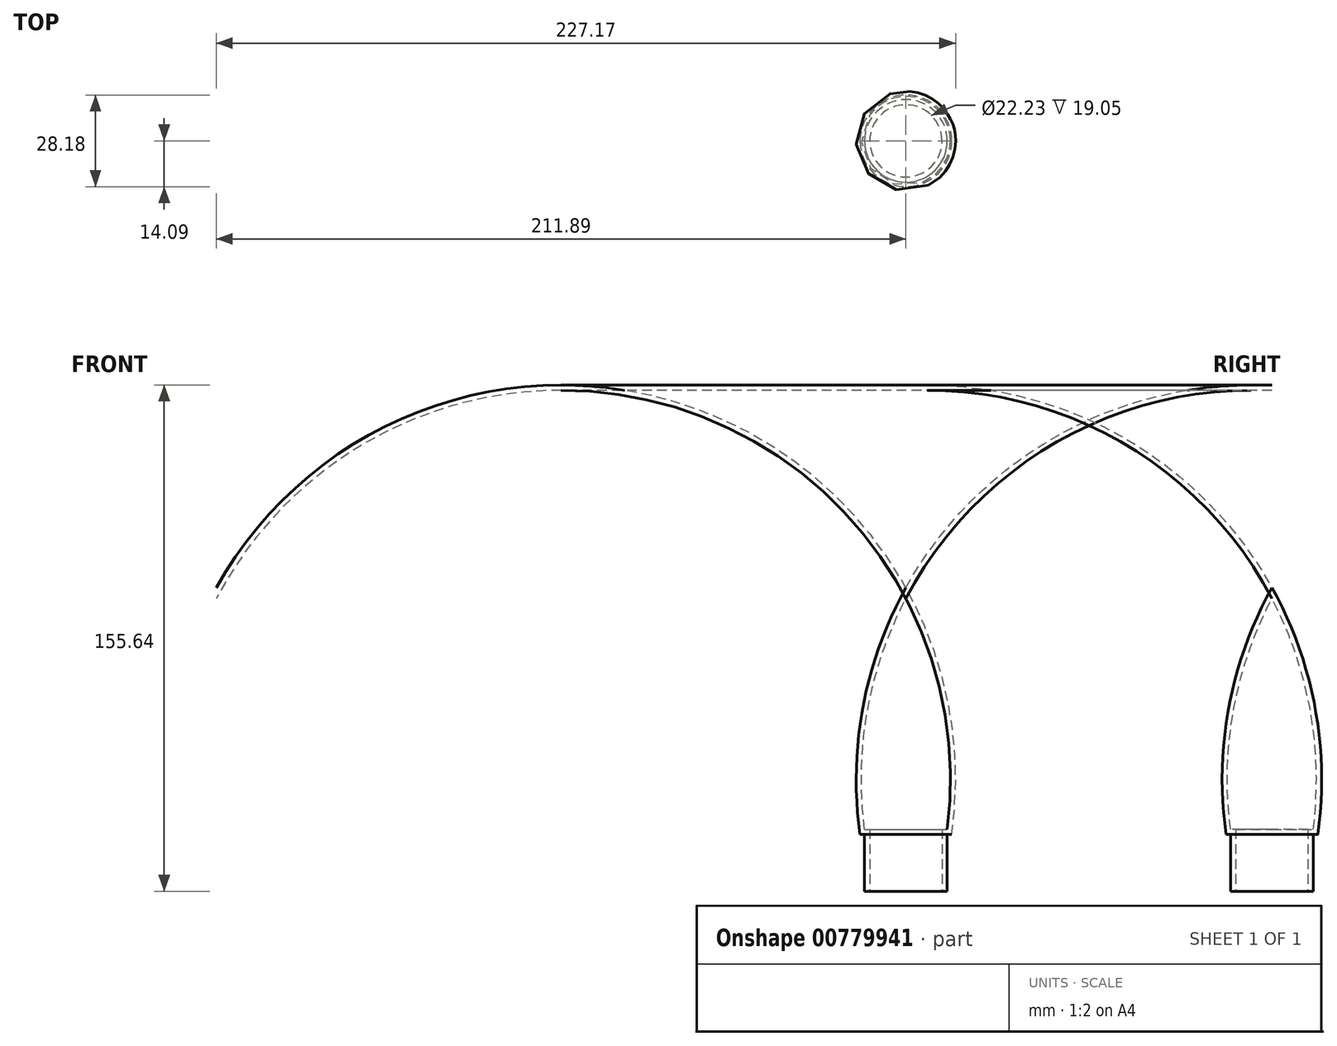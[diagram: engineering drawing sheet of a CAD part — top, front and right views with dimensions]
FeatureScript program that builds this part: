
annotation { "Feature Type Name" : "Feature", "Feature Type Description" : "" }
export const myFeature = defineFeature(function(context is Context, id is Id, definition is map)
    precondition{}
    {
        {
            var Q0;
            Q0=qCreatedBy(makeId("Front.planeOp"),FACE);
            var sketch = newSketch(context, id + "F0", { "sketchPlane" : qUnion([Q0])});
            skLineSegment(sketch, "E0", {"start": v(0, 0) * mm, "end": v(0, 90) * mm});
            skLineSegment(sketch, "E1", {"start": v(11.11, 0) * mm, "end": v(11.11, 19.05) * mm});
            skLineSegment(sketch, "E2", {"start": v(11.11, 19.05) * mm, "end": v(12.7, 19.05) * mm});
            skArc(sketch, "E3", {"start": v(12.7, 19.05) * mm, "mid": v(11.82, 55.5) * mm, "end": v(0, 90) * mm});
            skArc(sketch, "E4.0", {"start": v(14.09, 17.46) * mm, "mid": v(13.24, 56.55) * mm, "end": v(0, 93.33) * mm});
            skLineSegment(sketch, "E4.1", {"start": v(12.7, 17.46) * mm, "end": v(14.09, 17.46) * mm});
            skLineSegment(sketch, "E4.2", {"start": v(12.7, 0) * mm, "end": v(12.7, 17.46) * mm});
            skLineSegment(sketch, "E5", {"start": v(11.11, 0) * mm, "end": v(12.7, 0) * mm});
            skLineSegment(sketch, "E6", {"start": v(0, 90) * mm, "end": v(0, 93.33) * mm});
            skSolve(sketch);
        }
        {
            var Q0;
            Q0=makeQuery(id+"F0.imprint","IMPRINT",FACE,{"disambiguationData":[TD([[makeQuery(id+"F0.imprint","IMPRINT",EDGE,{"derivedFrom":sQuery(id+"F0.wireOp",EDGE,"E1")}),-1.0]])]});
            var Q1;
            Q1=sQuery(id+"F0.wireOp",EDGE,"E0");
            revolve(context, id + "F1", {"surfaceOperationType" : NewSurfaceOperationType.NEW, "entities" : qUnion([Q0]), "axis" : qUnion([Q1]), "revolveType" : RevolveType.FULL});
        }
    });
